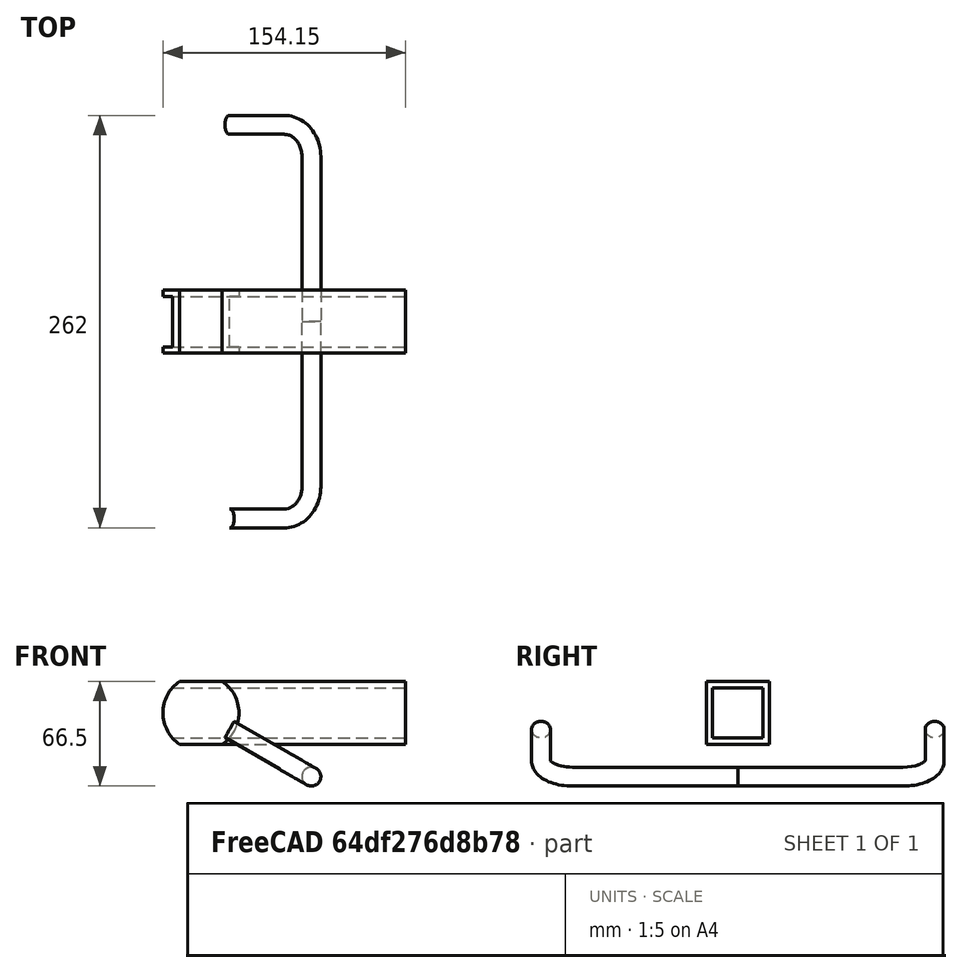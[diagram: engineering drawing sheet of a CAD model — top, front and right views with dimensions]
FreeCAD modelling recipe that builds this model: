
FCSTD DOCUMENT  (FreeCAD 0.21R33771 (Git))
Label: Haltegriff_FEM_RC_handle
License: All rights reserved
LicenseURL: https://en.wikipedia.org/wiki/All_rights_reserved
objects: Part::FeaturePython×7, Sketcher::SketchObject×5, Part::Feature×1, Part::Sweep×1, App::DocumentObjectGroup×1, App::MaterialObjectPython×1, Fem::ConstraintFixed×1, Fem::ConstraintForce×1, Fem::FemSolverObjectPython×1, Fem::FemMeshObjectPython×1, Fem::FemAnalysis×1
note: 14 computed .brp shape members not serialized (recipe doc carries the construction recipe); baked Part::Feature solids carry a one-line shape summary decoded from their .brp

FEATURE [Sketcher::SketchObject] Sketch
  FullyConstrained = false
  MapMode = 5
  Placement = pos=(0,0,0) rot=(1,0,0;1.5708rad)
  sketch-geometry (4):
    g0: LineSegment StartX=-70 StartY=-58.8 StartZ=0 EndX=-70 EndY=-66.8 EndZ=0
    g1: LineSegment StartX=-70 StartY=-66.8 StartZ=0 EndX=70 EndY=-66.8 EndZ=0
    g2: LineSegment StartX=70 StartY=-66.8 StartZ=0 EndX=70 EndY=-58.8 EndZ=0
    g3: LineSegment StartX=70 StartY=-58.8 StartZ=0 EndX=-70 EndY=-58.8 EndZ=0
  constraints (10):
    c: Coincident(g0,g1)
    c: Coincident(g1,g2)
    c: Coincident(g2,g3)
    c: Coincident(g3,g0)
    c: Vertical(g0)
    c: Vertical(g2)
    c: Horizontal(g3)
    c: Symmetric(g0,g1,g-2)
    c: DistanceY(g2,g2) = 8
    c: DistanceX(g1,g1) = 140
FEATURE [Sketcher::SketchObject] Sketch001
  FullyConstrained = false
  MapMode = 5
  Placement = pos=(0,0,0) rot=(1,0,0;1.5708rad)
  sketch-geometry (16):
    g0: LineSegment StartX=64.9 StartY=-58.8 StartZ=0 EndX=64.9 EndY=-53.7 EndZ=0
    g1: LineSegment StartX=64.9 StartY=-53.7 StartZ=0 EndX=70 EndY=-53.7 EndZ=0
    g2: LineSegment StartX=70 StartY=-53.7 StartZ=0 EndX=70 EndY=-45.7 EndZ=0
    g3: LineSegment StartX=70 StartY=-45.7 StartZ=0 EndX=10 EndY=-45.7 EndZ=0
    g4: LineSegment StartX=10 StartY=-45.7 StartZ=0 EndX=10 EndY=-53.7 EndZ=0
    g5: LineSegment StartX=10 StartY=-53.7 StartZ=0 EndX=59.8 EndY=-53.7 EndZ=0
    g6: LineSegment StartX=59.8 StartY=-53.7 StartZ=0 EndX=59.8 EndY=-58.8 EndZ=0
    g7: LineSegment StartX=59.8 StartY=-58.8 StartZ=0 EndX=64.9 EndY=-58.8 EndZ=0
    g8: LineSegment StartX=-64.9 StartY=-58.8 StartZ=0 EndX=-64.9 EndY=-53.7 EndZ=0
    g9: LineSegment StartX=-64.9 StartY=-53.7 StartZ=0 EndX=-70 EndY=-53.7 EndZ=0
    g10: LineSegment StartX=-70 StartY=-53.7 StartZ=0 EndX=-70 EndY=-45.7 EndZ=0
    g11: LineSegment StartX=-70 StartY=-45.7 StartZ=0 EndX=-10 EndY=-45.7 EndZ=0
    g12: LineSegment StartX=-10 StartY=-45.7 StartZ=0 EndX=-10 EndY=-53.7 EndZ=0
    g13: LineSegment StartX=-10 StartY=-53.7 StartZ=0 EndX=-59.8 EndY=-53.7 EndZ=0
    g14: LineSegment StartX=-59.8 StartY=-53.7 StartZ=0 EndX=-59.8 EndY=-58.8 EndZ=0
    g15: LineSegment StartX=-59.8 StartY=-58.8 StartZ=0 EndX=-64.9 EndY=-58.8 EndZ=0
  constraints (41):
    c: Coincident(g0,g1)
    c: Coincident(g1,g2)
    c: Vertical(g2)
    c: Coincident(g2,g3)
    c: Horizontal(g3)
    c: Coincident(g3,g4)
    c: Vertical(g4)
    c: Coincident(g4,g5)
    c: Horizontal(g5)
    c: Coincident(g5,g6)
    c: Vertical(g6)
    c: Coincident(g6,g7)
    c: Coincident(g7,g0)
    c: Coincident(g8,g9)
    c: Coincident(g9,g10)
    c: Vertical(g10)
    c: Coincident(g10,g11)
    c: Horizontal(g11)
    c: Coincident(g11,g12)
    c: Coincident(g12,g13)
    c: Horizontal(g13)
    c: Coincident(g13,g14)
    c: Coincident(g14,g15)
    c: Coincident(g15,g8)
    c: Horizontal(g15)
    c: Vertical(g8)
    c: Vertical(g14)
    c: Horizontal(g9)
    c: Horizontal(g8,g13)
    c: Equal(g14,g15)
    c: Equal(g8,g9)
    c: Vertical(g12)
    c: DistanceX(g11,g11) = 60
    c: Horizontal(g7)
    c: Vertical(g0)
    c: Horizontal(g0,g5)
    c: Equal(g12,g2)
    c: Equal(g3,g11)
    c: Horizontal(g1)
    c: Equal(g1,g7)
    c: Equal(g7,g0)
FEATURE [Part::Feature] Defeatured003  label="QR40x4"
  shape: bbox 300 x 40 x 40 mm, 10 faces (baked)
FEATURE [Sketcher::SketchObject] Sketch002
  FullyConstrained = true
  Placement = pos=(0,0,0) rot=(1,0,0;1.5708rad)
  sketch-geometry (3):
    g0: Circle CenterX=0 CenterY=0 CenterZ=0 NormalX=0 NormalY=0 NormalZ=1 AngleXU=0 Radius=24.15
    g1: Circle CenterX=0 CenterY=0 CenterZ=0 NormalX=0 NormalY=0 NormalZ=1 AngleXU=0 Radius=20.15
    g2: LineSegment StartX=20.15 StartY=0 StartZ=0 EndX=24.15 EndY=0 EndZ=0
  constraints (8):
    c: Diameter(g0) = 48.3
    c: Coincident(g0,g-1)
    c: Coincident(g1,g0)
    c: PointOnObject(g2,g1)
    c: PointOnObject(g2,g0)
    c: PointOnObject(g2,g-1)
    c: Horizontal(g2)
    c: DistanceX(g2,g2) = 4
FEATURE [Sketcher::SketchObject] Sketch003
  FullyConstrained = false
  sketch-geometry (10):
    g0: LineSegment StartX=0 StartY=195 StartZ=0 EndX=40 EndY=195 EndZ=0
    g1: LineSegment StartX=0 StartY=-55 StartZ=0 EndX=40 EndY=-55 EndZ=0
    g2: LineSegment StartX=60 StartY=175 StartZ=0 EndX=60 EndY=120 EndZ=0
    g3: LineSegment StartX=60 StartY=20 StartZ=0 EndX=60 EndY=-35 EndZ=0
    g4: ArcOfCircle CenterX=40 CenterY=175 CenterZ=0 NormalX=0 NormalY=0 NormalZ=1 AngleXU=0 Radius=20 StartAngle=0 EndAngle=1.5708
    g5: ArcOfCircle CenterX=40 CenterY=-35 CenterZ=0 NormalX=0 NormalY=0 NormalZ=1 AngleXU=0 Radius=20 StartAngle=4.71239 EndAngle=6.28319
    g6: LineSegment StartX=60 StartY=120 StartZ=0 EndX=60 EndY=70 EndZ=0
    g7: LineSegment StartX=60 StartY=70 StartZ=0 EndX=60 EndY=20 EndZ=0
    g8: LineSegment StartX=120.15 StartY=220 StartZ=0 EndX=0 EndY=195 EndZ=0
    g9: LineSegment StartX=120.15 StartY=-80 StartZ=0 EndX=0 EndY=-55 EndZ=0
  constraints (29):
    c: Horizontal(g0)
    c: Horizontal(g1)
    c: Vertical(g2)
    c: Coincident(g6,g2)
    c: Vertical(g3)
    c: Coincident(g7,g3)
    c: Equal(g2,g3)
    c: DistanceY(g7,g6) = 100
    c: Vertical(g0,g1)
    c: Vertical(g0,g1)
    c: DistanceY(g1,g0) = 250
    c: Coincident(g4,g0)
    c: Coincident(g4,g2)
    c: Coincident(g5,g3)
    c: Coincident(g5,g1)
    c: Vertical(g5,g1)
    c: Horizontal(g5,g3)
    c: Vertical(g4,g0)
    c: Horizontal(g4,g2)
    c: Radius(g4) = 20
    c: DistanceX(g0,g2) = 60
    c: Coincident(g6,g7)
    c: Vertical(g6)
    c: Vertical(g7)
    c: Equal(g6,g7)
    c: PointOnObject(g1,g-2)
    c: Coincident(g8,g0)
    c: Coincident(g9,g1)
    c: Equal(g9,g8)
FEATURE [Sketcher::SketchObject] Sketch004
  ExternalGeometry = -> [Sketch003]
  FullyConstrained = true
  Placement = pos=(0,0,0) rot=(0.57735,0.57735,0.57735;2.0944rad)
  sketch-geometry (1):
    g0: Circle CenterX=-55 CenterY=0 CenterZ=0 NormalX=0 NormalY=0 NormalZ=1 AngleXU=0 Radius=6
  constraints (2):
    c: Coincident(g0,g-3)
    c: Diameter(g0) = 12
FEATURE [Part::Sweep] Sweep
  Frenet = true
  Placement = pos=(118.187,1.4e-14,-97.3) rot=(0,1,0;0.523599rad)
  Sections = -> [Sketch004]
  Solid = true
  Spine = -> Sketch003 [Edge1,Edge2,Edge3,Edge4]
  Transition = 1
FEATURE [Part::FeaturePython] Clone  label="Sweep001"  # Draft clone (typed FeaturePython)
  AttacherType = Attacher::AttachEngine3D
  Fuse = false
  Objects = -> [Sweep]
  Placement = pos=(118.187,140,-97.3) rot=(0.965926,0,-0.258819;3.14159rad)
  Scale = (1,1,1)
FEATURE [Part::FeaturePython] Facebinder  # WARN: FeaturePython — macro-defined, semantics opaque (R4)
  Area = 45521.7
  Extrusion = 0
  RemoveSplitter = false
  Sew = false
FEATURE [Part::FeaturePython] Slice  # WARN: FeaturePython — macro-defined, semantics opaque (R4)
  Base = -> Defeatured003
  Mode = 1
  Tolerance = 0
  Tools = -> [Facebinder]
FEATURE [Part::FeaturePython] Slice_child1  label="Slice.1"  # WARN: FeaturePython — macro-defined, semantics opaque (R4)
  Base = -> Slice
  FilterType = 1
  Invert = false
  OverrideMaxVal = 0
  WindowFrom = 80
  WindowTo = 100
  items = 1
FEATURE [Part::FeaturePython] Slice_child2  label="Slice.2"  # WARN: FeaturePython — macro-defined, semantics opaque (R4)
  Base = -> Slice
  FilterType = 1
  Invert = false
  OverrideMaxVal = 0
  WindowFrom = 80
  WindowTo = 100
  items = 2
FEATURE [App::DocumentObjectGroup] GrExplode_Slice  label="Exploded Slice"
  Group = -> [Slice_child1,Slice_child2]
FEATURE [Part::FeaturePython] BooleanFragments  # WARN: FeaturePython — macro-defined, semantics opaque (R4)
  Mode = 2
  Objects = -> [Sweep,Clone]
  Tolerance = 0
FEATURE [Part::FeaturePython] CompoundFilter  # WARN: FeaturePython — macro-defined, semantics opaque (R4)
  Base = -> BooleanFragments
  FilterType = 3
  Invert = false
  OverrideMaxVal = 0
  WindowFrom = 80
  WindowTo = 100
FEATURE [App::MaterialObjectPython] MaterialSolid  label="S235"  # material (typed FeaturePython)
  Category = 0
  Material = AmbientColor=(0.0020, 0.0020, 0.0020, 1.0),Author=Juergen Riegel,AuthorAndLicense=CC-BY-3.0,CardName=CalculiX-Steel,Density=7.9e-06 kg/mm^3,+14 more (map truncated)
  UUID = 92589471-a6cb-4bbc-b748-d425a17dea7d
FEATURE [Fem::ConstraintFixed] ConstraintFixed
  NormalDirection = (-0.866025,0,0.5)
  Normals = (10) [(-0.866025,0,0.5),(-0.866025,0,0.5),(-0.866025,0,0.5),(-0.866025,0,0.5),(-0.866025,0,0.5),(-0.866025,0,0.5),(-0.866025,0,0.5),(-0.866025,0,0.5),+2 more]
  Points = (10) [(118.187,-49,-97.3),(115.187,-55,-102.496),(118.187,-55,-97.3),(121.187,-55,-92.1038),(118.187,-61,-97.3),(118.187,189,-97.3),(121.187,195,-92.1038),+3 more]
  References = -> [Sweep,Clone]
FEATURE [Fem::ConstraintForce] ConstraintForce001  label="Mannlast"
  DirectionVector = (0.866025,0,-0.5)
  Force = 1000
  NormalDirection = (0.866025,0,-0.5)
  Points = (16) [(164.952,20,-124.3),(175.344,20,-124.3),(170.148,20,-133.3),(164.952,20,-124.3),(164.952,36.6667,-124.3),(175.344,36.6667,-124.3),+10 more]
  References = -> [Sweep]
  Scale = 5
FEATURE [Fem::FemSolverObjectPython] SolverCcxTools  # FEM object (typed FeaturePython)
  AnalysisType = 0
  BeamReducedIntegration = true
  BeamShellResultOutput3D = true
  BucklingFactors = 1
  EigenmodeHighLimit = 1000000
  EigenmodeLowLimit = 0
  EigenmodesCount = 10
  GeometricalNonlinearity = 0
  IterationsControlParameterCutb = 0.25,0.5,0.75,0.85,,,1.5,
  IterationsControlParameterIter = 4,8,9,200,10,400,,200,,
  IterationsControlParameterTimeUse = false
  IterationsMaximum = 2000
  IterationsThermoMechMaximum = 2000
  IterationsUserDefinedIncrementations = false
  IterationsUserDefinedTimeStepLength = false
  MaterialNonlinearity = 0
  MatrixSolverType = 1
  ModelSpace = 0
  OutputFrequency = 1
  SplitInputWriter = true
  ThermoMechSteadyState = true
  ThermoMechType = 0
  TimeEnd = 1
  TimeInitialStep = 0.01
  TimeMaximumStep = 1
  TimeMinimumStep = 1e-05
FEATURE [Fem::FemMeshObjectPython] FEMMeshGmsh  # FEM object (typed FeaturePython)
  Algorithm2D = 0
  Algorithm3D = 0
  CharacteristicLengthMax = 20
  CharacteristicLengthMin = 0
  CoherenceMesh = true
  ElementDimension = 0
  ElementOrder = 1
  GeometryTolerance = 1e-06
  GroupsOfNodes = false
  HighOrderOptimize = 0
  MeshSizeFromCurvature = 12
  OptimizeNetgen = false
  OptimizeStd = true
  Part = -> CompoundFilter
  RecombinationAlgorithm = 0
  Recombine3DAll = false
  RecombineAll = false
  SecondOrderLinear = false
FEATURE [Fem::FemAnalysis] Analysis
  Group = -> [MaterialSolid,ConstraintFixed,ConstraintForce001,SolverCcxTools,FEMMeshGmsh]
